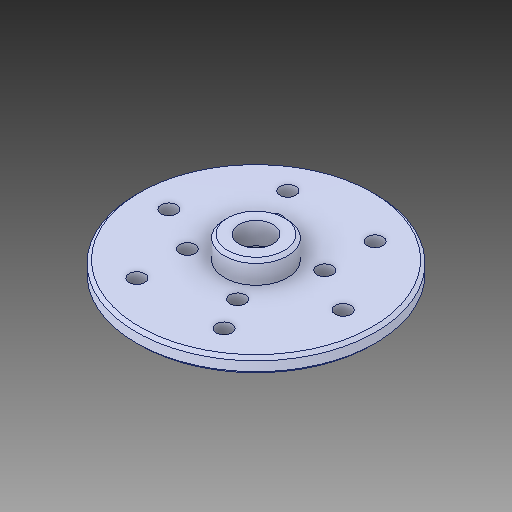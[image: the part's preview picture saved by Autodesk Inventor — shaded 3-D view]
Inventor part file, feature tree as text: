
AUTODESK INVENTOR PART (.ipt)
format: ipt  version: 2019 (Build 230136000, 136)  size: 154,624 bytes
history: native  units: in
note: dims shown in document units (in); Inventor stores cm internally (conversion verified against a paired STEP export)
features: chamfer x1
ambient origin geometry x8: Origin, YZ Plane, XZ Plane, XY Plane, X Axis, Y Axis, Z Axis, Center Point
bodies: Solid1 (feature_tree)
feature tree (1):
  chamfer  "Chamfer1"  [1 undecoded]
note: 1 required parameter value undecoded (feature->parameter linkage not recoverable at this tier; creation-order binding heuristic only, values carry confidence <= 0.55)
